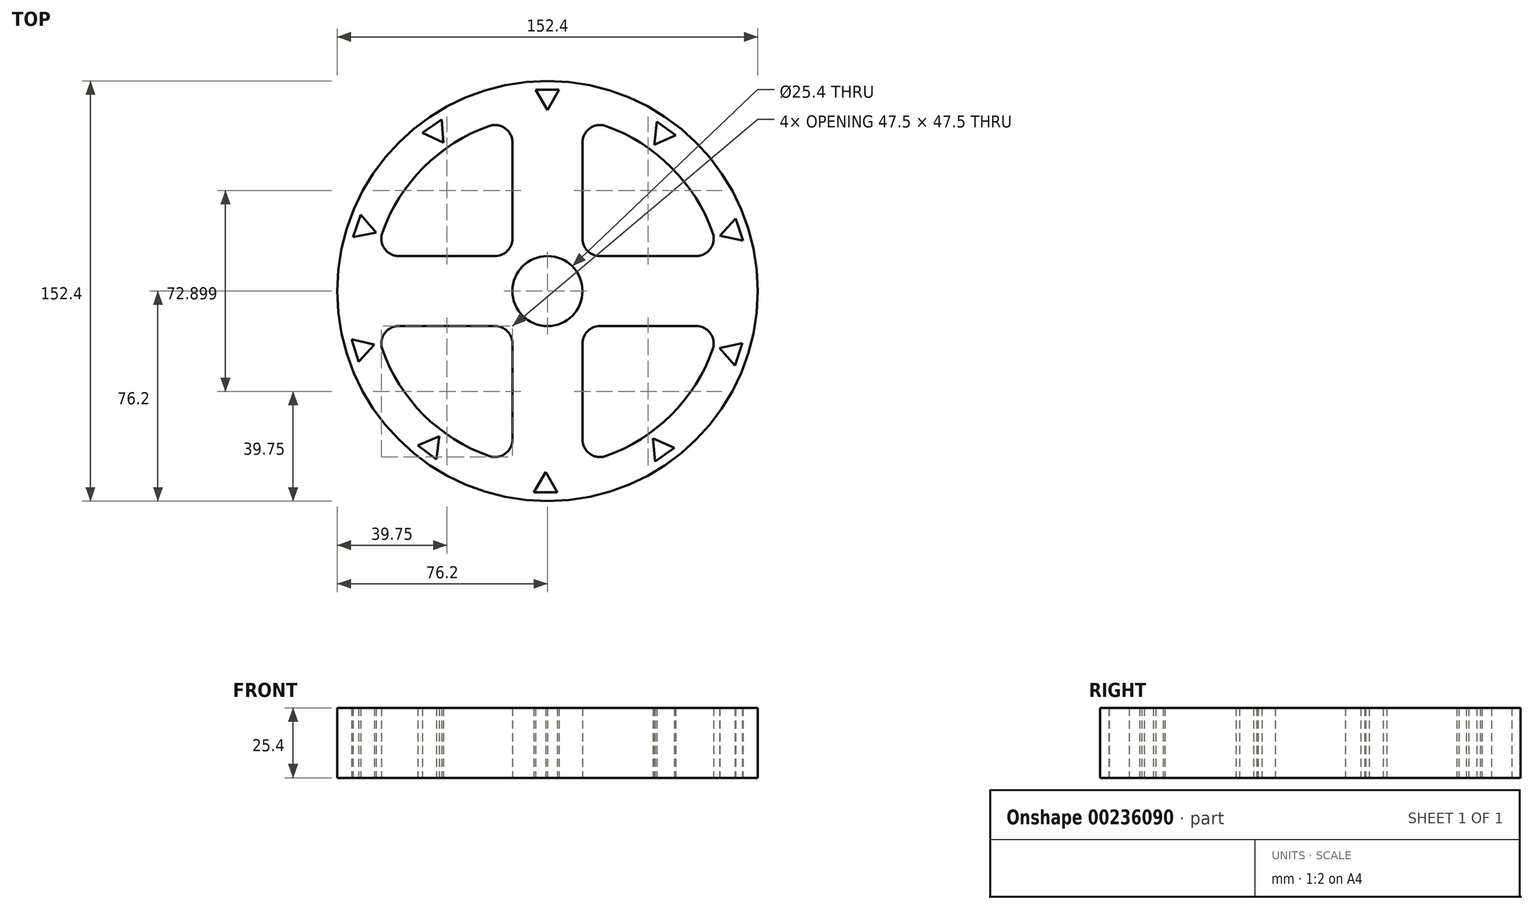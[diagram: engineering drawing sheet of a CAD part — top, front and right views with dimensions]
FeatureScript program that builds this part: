
annotation { "Feature Type Name" : "Feature", "Feature Type Description" : "" }
export const myFeature = defineFeature(function(context is Context, id is Id, definition is map)
    precondition{}
    {
        {
            var Q0;
            Q0=qCreatedBy(makeId("Top.planeOp"),FACE);
            var sketch = newSketch(context, id + "F0", { "sketchPlane" : qUnion([Q0])});
            skCircle(sketch, "E0", {"center": v(0, 0) * mm, "radius": 76.2 * mm});
            skArc(sketch, "E1", {"start": v(-59.87, -21.17) * mm, "mid": v(-44.9, -44.9) * mm, "end": v(-21.17, -59.87) * mm});
            skCircle(sketch, "E2", {"center": v(0, 0) * mm, "radius": 12.7 * mm});
            skLineSegment(sketch, "E3", {"start": v(0, 0) * mm, "end": v(0, 63.5) * mm});
            skLineSegment(sketch, "E4.0", {"start": v(12.7, 19.05) * mm, "end": v(12.7, 53.88) * mm});
            skLineSegment(sketch, "E5.0", {"start": v(-12.7, 19.05) * mm, "end": v(-12.7, 53.88) * mm});
            skLineSegment(sketch, "E6", {"start": v(0, 0) * mm, "end": v(-63.5, 0) * mm});
            skLineSegment(sketch, "E7", {"start": v(0, 0) * mm, "end": v(63.5, 0) * mm});
            skLineSegment(sketch, "E8", {"start": v(0, 0) * mm, "end": v(0, -63.5) * mm});
            skLineSegment(sketch, "E9.0", {"start": v(19.05, -12.7) * mm, "end": v(53.88, -12.7) * mm});
            skLineSegment(sketch, "E10.0", {"start": v(19.05, 12.7) * mm, "end": v(53.88, 12.7) * mm});
            skLineSegment(sketch, "E11.0", {"start": v(-12.7, -19.05) * mm, "end": v(-12.7, -53.88) * mm});
            skLineSegment(sketch, "E12.0", {"start": v(12.7, -19.05) * mm, "end": v(12.7, -53.88) * mm});
            skLineSegment(sketch, "E13.0", {"start": v(-19.05, 12.7) * mm, "end": v(-53.88, 12.7) * mm});
            skLineSegment(sketch, "E14.0", {"start": v(-19.05, -12.7) * mm, "end": v(-53.88, -12.7) * mm});
            skLineSegment(sketch, "E15.trimOffspring", {"start": v(-75.13, 12.7) * mm, "end": v(-76.2, 12.7) * mm});
            skLineSegment(sketch, "E16.trimOffspring", {"start": v(-75.13, -12.7) * mm, "end": v(-76.2, -12.7) * mm});
            skArc(sketch, "E17.trimOffspring", {"start": v(59.87, 21.17) * mm, "mid": v(44.9, 44.9) * mm, "end": v(21.17, 59.87) * mm});
            skLineSegment(sketch, "E18.trimOffspring", {"start": v(75.13, -12.7) * mm, "end": v(76.2, -12.7) * mm});
            skLineSegment(sketch, "E19.trimOffspring", {"start": v(75.13, 12.7) * mm, "end": v(76.2, 12.7) * mm});
            skLineSegment(sketch, "E20.trimOffspring", {"start": v(12.7, -75.13) * mm, "end": v(12.7, -76.2) * mm});
            skLineSegment(sketch, "E21.trimOffspring", {"start": v(-12.7, -75.13) * mm, "end": v(-12.7, -76.2) * mm});
            skArc(sketch, "E22.trimOffspring", {"start": v(21.17, -59.87) * mm, "mid": v(44.9, -44.9) * mm, "end": v(59.87, -21.17) * mm});
            skLineSegment(sketch, "E23.trimOffspring", {"start": v(-12.7, 75.13) * mm, "end": v(-12.7, 76.2) * mm});
            skLineSegment(sketch, "E24.trimOffspring", {"start": v(12.7, 75.13) * mm, "end": v(12.7, 76.2) * mm});
            skArc(sketch, "E25.trimOffspring", {"start": v(-21.17, 59.87) * mm, "mid": v(-44.9, 44.9) * mm, "end": v(-59.87, 21.17) * mm});
            skCircle(sketch, "E26.cCircle", {"center": v(0, 70.58) * mm, "radius": 2.45 * mm, "construction": true});
            skLineSegment(sketch, "E26.0", {"start": v(4.24, 73.03) * mm, "end": v(0, 65.68) * mm});
            skLineSegment(sketch, "E26.1", {"start": v(0, 65.68) * mm, "end": v(-4.24, 73.03) * mm});
            skLineSegment(sketch, "E26.2", {"start": v(-4.24, 73.03) * mm, "end": v(4.24, 73.03) * mm});
            skPoint(sketch, "E26.0.midPoint", {"position": v(2.12, 69.35) * mm});
            skLineSegment(sketch, "E27.1.0", {"start": v(39.61, 61.5) * mm, "end": v(46.47, 56.5) * mm});
            skLineSegment(sketch, "E27.1.1", {"start": v(46.47, 56.5) * mm, "end": v(38.7, 53.06) * mm});
            skLineSegment(sketch, "E27.1.2", {"start": v(38.7, 53.06) * mm, "end": v(39.61, 61.5) * mm});
            skLineSegment(sketch, "E27.2.0", {"start": v(68.25, 26.34) * mm, "end": v(70.84, 18.26) * mm});
            skLineSegment(sketch, "E27.2.1", {"start": v(70.84, 18.26) * mm, "end": v(62.54, 20.05) * mm});
            skLineSegment(sketch, "E27.2.2", {"start": v(62.54, 20.05) * mm, "end": v(68.25, 26.34) * mm});
            skLineSegment(sketch, "E27.3.0", {"start": v(70.66, -18.94) * mm, "end": v(67.99, -27) * mm});
            skLineSegment(sketch, "E27.3.1", {"start": v(67.99, -27) * mm, "end": v(62.34, -20.66) * mm});
            skLineSegment(sketch, "E27.3.2", {"start": v(62.34, -20.66) * mm, "end": v(70.66, -18.94) * mm});
            skLineSegment(sketch, "E27.4.0", {"start": v(45.92, -56.94) * mm, "end": v(39.01, -61.88) * mm});
            skLineSegment(sketch, "E27.4.1", {"start": v(39.01, -61.88) * mm, "end": v(38.2, -53.43) * mm});
            skLineSegment(sketch, "E27.4.2", {"start": v(38.2, -53.43) * mm, "end": v(45.92, -56.94) * mm});
            skLineSegment(sketch, "E27.5.0", {"start": v(3.54, -73.07) * mm, "end": v(-4.95, -72.98) * mm});
            skLineSegment(sketch, "E27.5.1", {"start": v(-4.95, -72.98) * mm, "end": v(-0.64, -65.67) * mm});
            skLineSegment(sketch, "E27.5.2", {"start": v(-0.64, -65.67) * mm, "end": v(3.54, -73.07) * mm});
            skLineSegment(sketch, "E27.6.0", {"start": v(-40.2, -61.11) * mm, "end": v(-47.01, -56.04) * mm});
            skLineSegment(sketch, "E27.6.1", {"start": v(-47.01, -56.04) * mm, "end": v(-39.22, -52.68) * mm});
            skLineSegment(sketch, "E27.6.2", {"start": v(-39.22, -52.68) * mm, "end": v(-40.2, -61.11) * mm});
            skLineSegment(sketch, "E27.7.0", {"start": v(-68.5, -25.68) * mm, "end": v(-71.01, -17.57) * mm});
            skLineSegment(sketch, "E27.7.1", {"start": v(-71.01, -17.57) * mm, "end": v(-62.73, -19.45) * mm});
            skLineSegment(sketch, "E27.7.2", {"start": v(-62.73, -19.45) * mm, "end": v(-68.5, -25.68) * mm});
            skLineSegment(sketch, "E27.8.0", {"start": v(-70.47, 19.63) * mm, "end": v(-67.72, 27.66) * mm});
            skLineSegment(sketch, "E27.8.1", {"start": v(-67.72, 27.66) * mm, "end": v(-62.14, 21.26) * mm});
            skLineSegment(sketch, "E27.8.2", {"start": v(-62.14, 21.26) * mm, "end": v(-70.47, 19.63) * mm});
            skLineSegment(sketch, "E27.9.0", {"start": v(-45.36, 57.39) * mm, "end": v(-38.41, 62.26) * mm});
            skLineSegment(sketch, "E27.9.1", {"start": v(-38.41, 62.26) * mm, "end": v(-37.67, 53.8) * mm});
            skLineSegment(sketch, "E27.9.2", {"start": v(-37.67, 53.8) * mm, "end": v(-45.36, 57.39) * mm});
            skLineSegment(sketch, "E27.anchor1", {"start": v(0, 0) * mm, "end": v(-4.24, 73.03) * mm, "construction": true});
            skLineSegment(sketch, "E27.anchor2", {"start": v(0, 0) * mm, "end": v(-45.36, 57.39) * mm, "construction": true});
            skPoint(sketch, "E28.visualSharp", {"position": v(-12.7, 12.7) * mm});
            skArc(sketch, "E28.filletArc", {"start": v(-19.05, 12.7) * mm, "mid": v(-14.56, 14.56) * mm, "end": v(-12.7, 19.05) * mm});
            skPoint(sketch, "E29.visualSharp", {"position": v(12.7, 12.7) * mm});
            skArc(sketch, "E29.filletArc", {"start": v(12.7, 19.05) * mm, "mid": v(14.56, 14.56) * mm, "end": v(19.05, 12.7) * mm});
            skPoint(sketch, "E30.visualSharp", {"position": v(12.7, -12.7) * mm});
            skArc(sketch, "E30.filletArc", {"start": v(19.05, -12.7) * mm, "mid": v(14.56, -14.56) * mm, "end": v(12.7, -19.05) * mm});
            skPoint(sketch, "E31.visualSharp", {"position": v(-12.7, -12.7) * mm});
            skArc(sketch, "E31.filletArc", {"start": v(-12.7, -19.05) * mm, "mid": v(-14.56, -14.56) * mm, "end": v(-19.05, -12.7) * mm});
            skPoint(sketch, "E32.visualSharp", {"position": v(12.7, 62.22) * mm});
            skArc(sketch, "E32.filletArc", {"start": v(21.17, 59.87) * mm, "mid": v(15.38, 59.07) * mm, "end": v(12.7, 53.88) * mm});
            skPoint(sketch, "E33.visualSharp", {"position": v(-12.7, 62.22) * mm});
            skArc(sketch, "E33.filletArc", {"start": v(-12.7, 53.88) * mm, "mid": v(-15.38, 59.07) * mm, "end": v(-21.17, 59.87) * mm});
            skPoint(sketch, "E34.visualSharp", {"position": v(-62.22, 12.7) * mm});
            skArc(sketch, "E34.filletArc", {"start": v(-59.87, 21.17) * mm, "mid": v(-59.07, 15.38) * mm, "end": v(-53.88, 12.7) * mm});
            skPoint(sketch, "E35.visualSharp", {"position": v(62.22, 12.7) * mm});
            skArc(sketch, "E35.filletArc", {"start": v(53.88, 12.7) * mm, "mid": v(59.07, 15.38) * mm, "end": v(59.87, 21.17) * mm});
            skPoint(sketch, "E36.visualSharp", {"position": v(62.22, -12.7) * mm});
            skArc(sketch, "E36.filletArc", {"start": v(59.87, -21.17) * mm, "mid": v(59.07, -15.38) * mm, "end": v(53.88, -12.7) * mm});
            skPoint(sketch, "E37.visualSharp", {"position": v(12.7, -62.22) * mm});
            skArc(sketch, "E37.filletArc", {"start": v(12.7, -53.88) * mm, "mid": v(15.38, -59.07) * mm, "end": v(21.17, -59.87) * mm});
            skPoint(sketch, "E38.visualSharp", {"position": v(-12.7, -62.22) * mm});
            skArc(sketch, "E38.filletArc", {"start": v(-21.17, -59.87) * mm, "mid": v(-15.38, -59.07) * mm, "end": v(-12.7, -53.88) * mm});
            skPoint(sketch, "E39.visualSharp", {"position": v(-62.22, -12.7) * mm});
            skArc(sketch, "E39.filletArc", {"start": v(-53.88, -12.7) * mm, "mid": v(-59.07, -15.38) * mm, "end": v(-59.87, -21.17) * mm});
            skSolve(sketch);
        }
        {
            var Q0;
            Q0 = qSketchRegion(id + "F0", true);
            extrude(context, id + "F1", {"entities" : qUnion([Q0]), "endBound" : BoundingType.SYMMETRIC, "depth" : 25.4 * mm});
        }
    });
